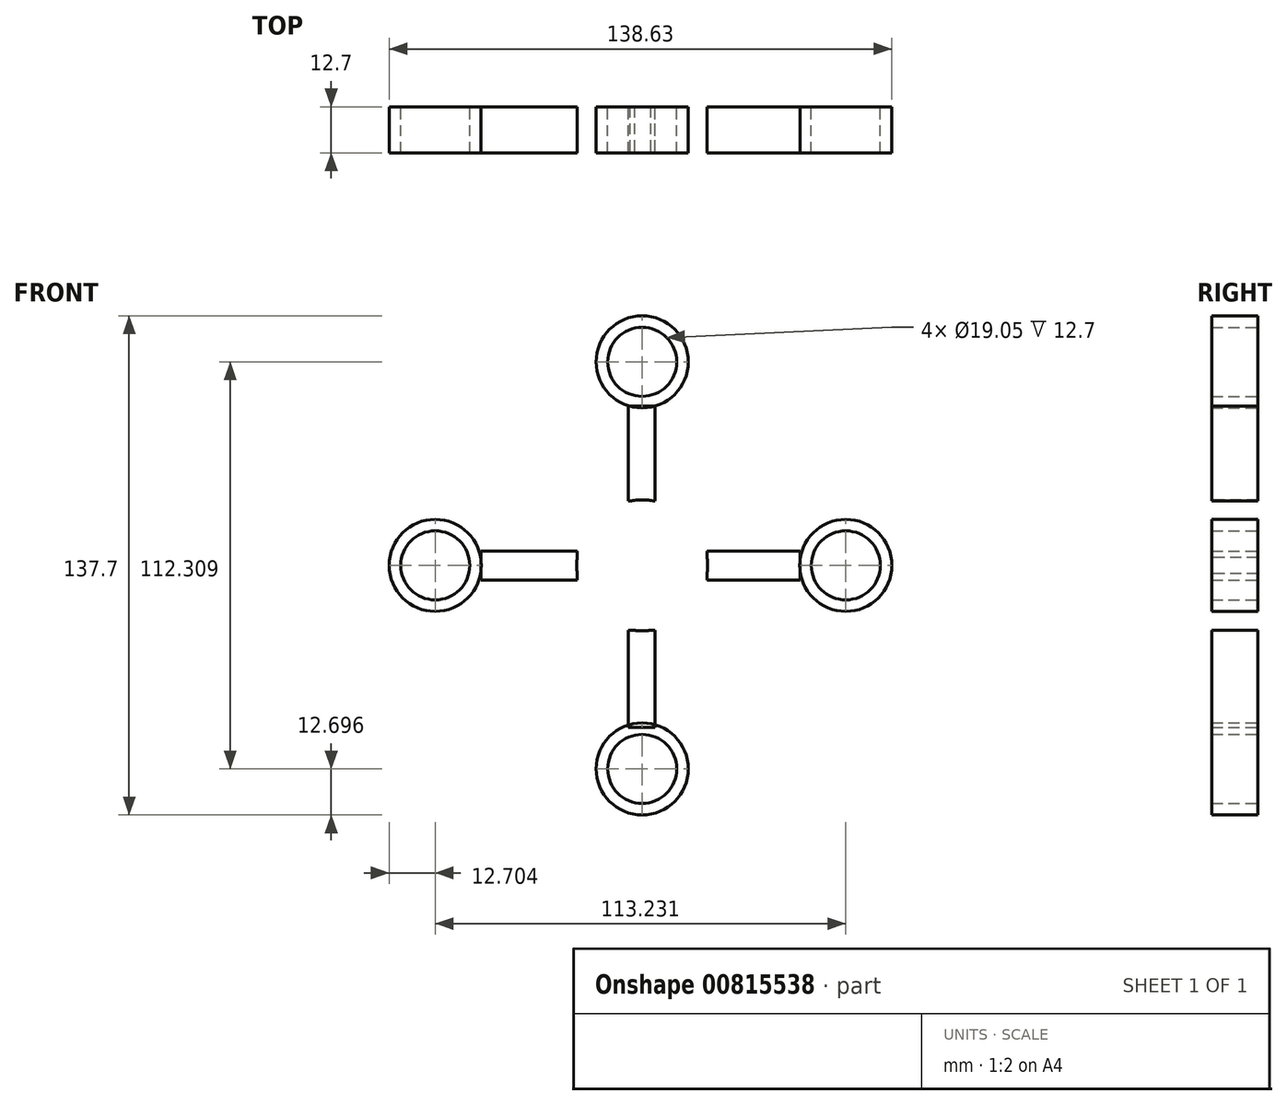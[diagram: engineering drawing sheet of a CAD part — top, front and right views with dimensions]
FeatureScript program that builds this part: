
annotation { "Feature Type Name" : "Feature", "Feature Type Description" : "" }
export const myFeature = defineFeature(function(context is Context, id is Id, definition is map)
    precondition{}
    {
        {
            var Q0;
            Q0=qCreatedBy(makeId("Front.planeOp"),FACE);
            var sketch = newSketch(context, id + "F0", { "sketchPlane" : qUnion([Q0])});
            skCircle(sketch, "E0", {"center": v(0, 0) * mm, "radius": 18.05 * mm});
            skLineSegment(sketch, "E1", {"start": v(-18.05, 0) * mm, "end": v(-43.45, 0) * mm});
            skCircle(sketch, "E2", {"center": v(-57.08, 0) * mm, "radius": 12.7 * mm});
            skCircle(sketch, "E3", {"center": v(0, 56.15) * mm, "radius": 12.7 * mm});
            skCircle(sketch, "E4", {"center": v(56.15, 0) * mm, "radius": 12.7 * mm});
            skCircle(sketch, "E5", {"center": v(0, -56.15) * mm, "radius": 12.7 * mm});
            skLineSegment(sketch, "E6", {"start": v(0, -18.05) * mm, "end": v(0, -43.45) * mm});
            skLineSegment(sketch, "E7", {"start": v(18.05, 0) * mm, "end": v(43.45, 0) * mm});
            skLineSegment(sketch, "E8", {"start": v(0, 18.05) * mm, "end": v(0, 43.45) * mm});
            skCircle(sketch, "E9", {"center": v(0, 0) * mm, "radius": 14.5 * mm});
            skCircle(sketch, "E10", {"center": v(-57.08, 0) * mm, "radius": 9.53 * mm});
            skCircle(sketch, "E11", {"center": v(0, -56.15) * mm, "radius": 9.53 * mm});
            skCircle(sketch, "E12", {"center": v(0, 56.15) * mm, "radius": 9.53 * mm});
            skCircle(sketch, "E13", {"center": v(56.15, 0) * mm, "radius": 9.53 * mm});
            skSolve(sketch);
        }
        {
            var Q0;
            Q0=makeQuery(id+"F0.imprint","IMPRINT",FACE,{"disambiguationData":[TD([[makeQuery(id+"F0.imprint","IMPRINT",EDGE,{"derivedFrom":sQuery(id+"F0.wireOp",EDGE,"E2")}),1.0]])]});
            var Q1;
            {var subQ0=sQuery(id+"F0.wireOp",EDGE,"E0");var subQ1=makeQuery(id+"F0.imprint","IMPRINT",VERTEX,{"disambiguationData":[OD(2.0)],"derivedFrom":subQ0});Q1=makeQuery(id+"F0.imprint","IMPRINT",FACE,{"disambiguationData":[TD([[makeQuery(id+"F0.imprint","IMPRINT",EDGE,{"disambiguationData":[TD([[subQ1,-1.0]])],"derivedFrom":subQ0}),1.0]])]});}
            var Q2;
            Q2=makeQuery(id+"F0.imprint","IMPRINT",FACE,{"disambiguationData":[TD([[makeQuery(id+"F0.imprint","IMPRINT",EDGE,{"derivedFrom":sQuery(id+"F0.wireOp",EDGE,"E3")}),1.0]])]});
            var Q3;
            Q3=makeQuery(id+"F0.imprint","IMPRINT",FACE,{"disambiguationData":[TD([[makeQuery(id+"F0.imprint","IMPRINT",EDGE,{"derivedFrom":sQuery(id+"F0.wireOp",EDGE,"E4")}),1.0]])]});
            var Q4;
            Q4=makeQuery(id+"F0.imprint","IMPRINT",FACE,{"disambiguationData":[TD([[makeQuery(id+"F0.imprint","IMPRINT",EDGE,{"derivedFrom":sQuery(id+"F0.wireOp",EDGE,"E5")}),1.0]])]});
            extrude(context, id + "F1", {"entities" : qUnion([Q0, Q1, Q2, Q3, Q4]), "depth" : 12.7 * mm, "offsetDistance" : 25.4 * mm});
        }
        {
            var Q0;
            Q0=qCreatedBy(makeId("Front.planeOp"),FACE);
            var sketch = newSketch(context, id + "F2", { "sketchPlane" : qUnion([Q0])});
            skLineSegment(sketch, "E14.bottom", {"start": v(-3.89, 43.9) * mm, "end": v(3.5, 43.9) * mm});
            skLineSegment(sketch, "E14.top", {"start": v(-3.89, 17.73) * mm, "end": v(3.5, 17.73) * mm});
            skLineSegment(sketch, "E14.left", {"start": v(-3.89, 43.9) * mm, "end": v(-3.89, 17.73) * mm});
            skLineSegment(sketch, "E14.right", {"start": v(3.5, 43.9) * mm, "end": v(3.5, 17.73) * mm});
            skLineSegment(sketch, "E15.bottom", {"start": v(43.51, 3.89) * mm, "end": v(17.92, 3.89) * mm});
            skLineSegment(sketch, "E15.top", {"start": v(43.51, -4.08) * mm, "end": v(17.92, -4.08) * mm});
            skLineSegment(sketch, "E15.left", {"start": v(43.51, 3.89) * mm, "end": v(43.51, -4.08) * mm});
            skLineSegment(sketch, "E15.right", {"start": v(17.92, 3.89) * mm, "end": v(17.92, -4.08) * mm});
            skLineSegment(sketch, "E16.bottom", {"start": v(3.5, -44.65) * mm, "end": v(-3.89, -44.65) * mm});
            skLineSegment(sketch, "E16.top", {"start": v(3.5, -17.92) * mm, "end": v(-3.89, -17.92) * mm});
            skLineSegment(sketch, "E16.left", {"start": v(3.5, -44.65) * mm, "end": v(3.5, -17.92) * mm});
            skLineSegment(sketch, "E16.right", {"start": v(-3.89, -44.65) * mm, "end": v(-3.89, -17.92) * mm});
            skLineSegment(sketch, "E17.bottom", {"start": v(-44.46, 3.89) * mm, "end": v(-17.92, 3.89) * mm});
            skLineSegment(sketch, "E17.top", {"start": v(-44.46, -4.08) * mm, "end": v(-17.92, -4.08) * mm});
            skLineSegment(sketch, "E17.left", {"start": v(-44.46, 3.89) * mm, "end": v(-44.46, -4.08) * mm});
            skLineSegment(sketch, "E17.right", {"start": v(-17.92, 3.89) * mm, "end": v(-17.92, -4.08) * mm});
            skSolve(sketch);
        }
        {
            var Q0;
            Q0=makeQuery(id+"F2.imprint","IMPRINT",FACE,{"disambiguationData":[TD([[makeQuery(id+"F2.imprint","IMPRINT",EDGE,{"derivedFrom":sQuery(id+"F2.wireOp",EDGE,"E14.bottom")}),-1.0]])]});
            var Q1;
            Q1=makeQuery(id+"F2.imprint","IMPRINT",FACE,{"disambiguationData":[TD([[makeQuery(id+"F2.imprint","IMPRINT",EDGE,{"derivedFrom":sQuery(id+"F2.wireOp",EDGE,"E17.bottom")}),-1.0]])]});
            var Q2;
            Q2=makeQuery(id+"F2.imprint","IMPRINT",FACE,{"disambiguationData":[TD([[makeQuery(id+"F2.imprint","IMPRINT",EDGE,{"derivedFrom":sQuery(id+"F2.wireOp",EDGE,"E16.bottom")}),-1.0]])]});
            var Q3;
            Q3=makeQuery(id+"F2.imprint","IMPRINT",FACE,{"disambiguationData":[TD([[makeQuery(id+"F2.imprint","IMPRINT",EDGE,{"derivedFrom":sQuery(id+"F2.wireOp",EDGE,"E15.bottom")}),1.0]])]});
            extrude(context, id + "F3", {"entities" : qUnion([Q0, Q1, Q2, Q3]), "depth" : 12.7 * mm, "offsetDistance" : 25.4 * mm});
        }
        {
            var Q0;
            Q0=makeQuery(id+"F1.opExtrude","CAP_FACE",FACE,{"disambiguationData":[OSD([sQuery(id+"F0.wireOp",EDGE,"E0")])],"isStart":false});
            extrude(context, id + "F4", {"entities" : qUnion([Q0]), "operationType" : NewBodyOperationType.REMOVE, "oppositeDirection" : true, "depth" : 25.4 * mm, "offsetDistance" : 25.4 * mm});
        }
    });
